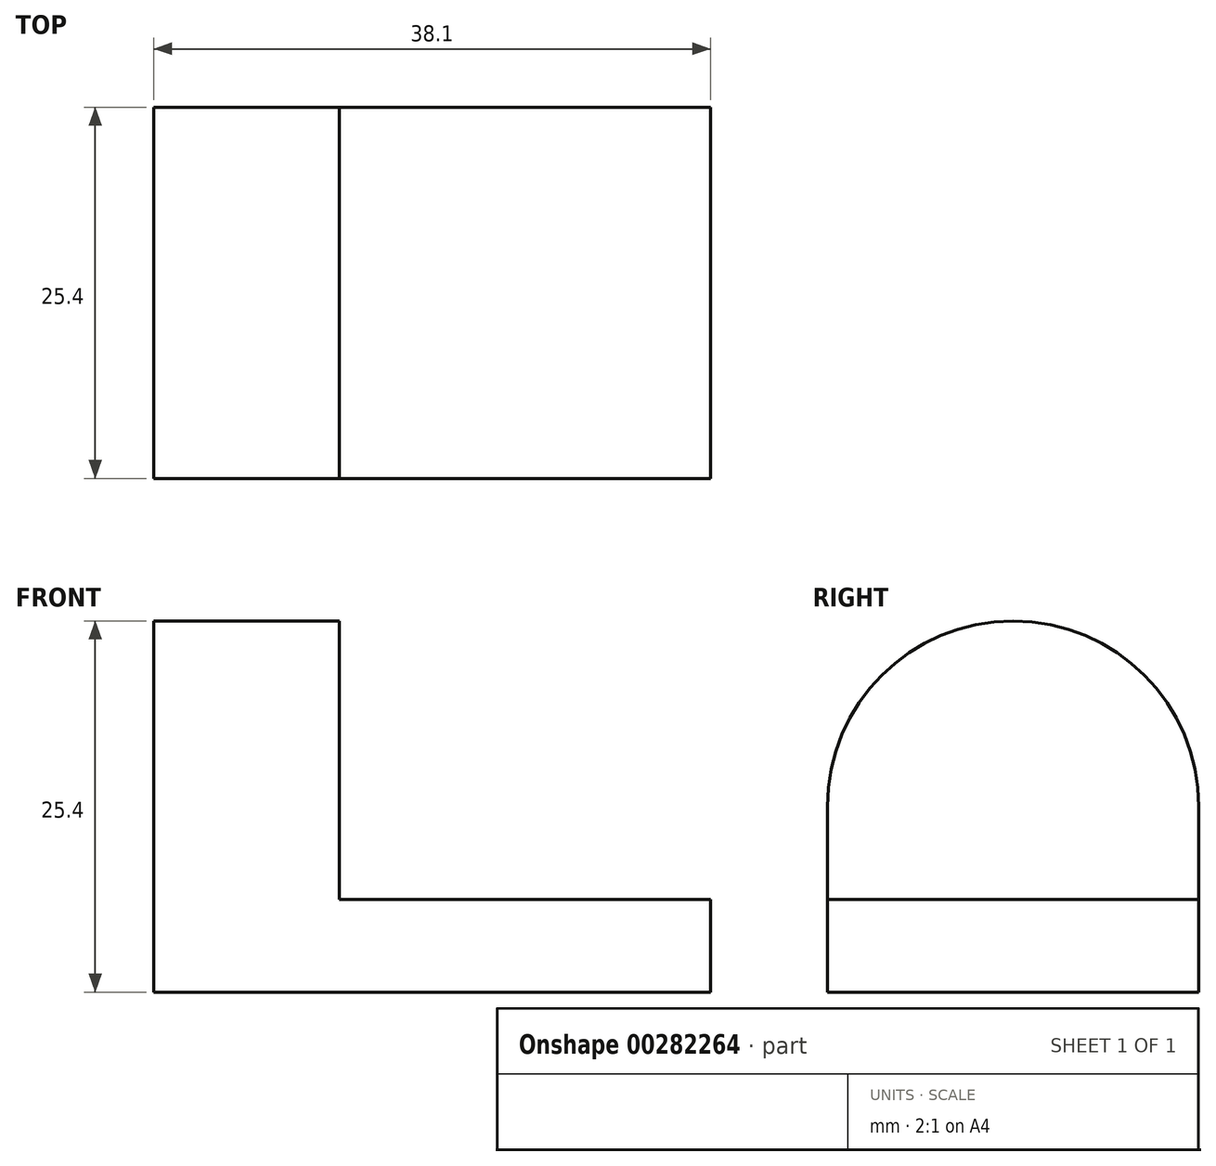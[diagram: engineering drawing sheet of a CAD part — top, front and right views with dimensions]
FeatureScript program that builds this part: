
annotation { "Feature Type Name" : "Feature", "Feature Type Description" : "" }
export const myFeature = defineFeature(function(context is Context, id is Id, definition is map)
    precondition{}
    {
        {
            var Q0;
            Q0=qCreatedBy(makeId("Top.planeOp"),FACE);
            var sketch = newSketch(context, id + "F0", { "sketchPlane" : qUnion([Q0])});
            skLineSegment(sketch, "E0.bottom", {"start": v(0, 0) * mm, "end": v(38.1, 0) * mm});
            skLineSegment(sketch, "E0.top", {"start": v(0, 25.4) * mm, "end": v(38.1, 25.4) * mm});
            skLineSegment(sketch, "E0.left", {"start": v(0, 0) * mm, "end": v(0, 25.4) * mm});
            skLineSegment(sketch, "E0.right", {"start": v(38.1, 0) * mm, "end": v(38.1, 25.4) * mm});
            skSolve(sketch);
        }
        {
            var Q0;
            Q0 = qSketchRegion(id + "F0", true);
            extrude(context, id + "F1", {"entities" : qUnion([Q0]), "depth" : 25.4 * mm});
        }
        {
            var Q0;
            Q0=makeQuery(id+"F1.opExtrude","SWEPT_FACE",FACE,{"disambiguationData":[OSD([sQuery(id+"F0.wireOp",EDGE,"E0.right")])]});
            var sketch = newSketch(context, id + "F2", { "sketchPlane" : qUnion([Q0])});
            skArc(sketch, "E1", {"start": v(25.4, 12.7) * mm, "mid": v(12.7, 25.4) * mm, "end": v(0, 12.7) * mm});
            skLineSegment(sketch, "E2", {"start": v(0, 0) * mm, "end": v(0, 6.35) * mm, "construction": true});
            skLineSegment(sketch, "E3", {"start": v(0, 6.35) * mm, "end": v(25.4, 6.35) * mm});
            skSolve(sketch);
        }
        {
            var Q0;
            {var subQ0=sQuery(id+"F2.wireOp",EDGE,"E1");var subQ1=sQuery(id+"F0.wireOp",EDGE,"E0.right");var subQ4=makeQuery(id+"F1.opExtrude","CAP_EDGE",EDGE,{"disambiguationData":[OSD([subQ1])],"isStart":false});var subQ5=makeQuery(id+"F2.imprint","INTERSECT",VERTEX,{"derivedFrom":[subQ4,subQ0]});Q0=makeQuery(id+"F2.imprint","IMPRINT",FACE,{"disambiguationData":[TD([[makeQuery(id+"F2.imprint","IMPRINT",EDGE,{"disambiguationData":[TD([[subQ5,1.0]])],"derivedFrom":subQ4}),-1.0]])]});}
            extrude(context, id + "F3", {"entities" : qUnion([Q0]), "operationType" : NewBodyOperationType.REMOVE, "endBound" : BoundingType.THROUGH_ALL, "oppositeDirection" : true, "depth" : 25.4 * mm});
        }
        {
            var Q0;
            {var subQ0=sQuery(id+"F2.wireOp",EDGE,"E1");var subQ1=sQuery(id+"F0.wireOp",EDGE,"E0.right");var subQ4=makeQuery(id+"F1.opExtrude","CAP_EDGE",EDGE,{"disambiguationData":[OSD([subQ1])],"isStart":false});var subQ5=makeQuery(id+"F2.imprint","INTERSECT",VERTEX,{"derivedFrom":[subQ4,subQ0]});Q0=makeQuery(id+"F2.imprint","IMPRINT",FACE,{"disambiguationData":[TD([[makeQuery(id+"F2.imprint","IMPRINT",EDGE,{"disambiguationData":[TD([[subQ5,-1.0]])],"derivedFrom":subQ4}),-1.0]])]});}
            extrude(context, id + "F4", {"entities" : qUnion([Q0]), "operationType" : NewBodyOperationType.REMOVE, "endBound" : BoundingType.THROUGH_ALL, "oppositeDirection" : true, "depth" : 25.4 * mm});
        }
        {
            var Q0;
            {var subQ0=sQuery(id+"F2.wireOp",EDGE,"E3");Q0=makeQuery(id+"F2.imprint","IMPRINT",FACE,{"disambiguationData":[TD([[makeQuery(id+"F2.imprint","IMPRINT",EDGE,{"derivedFrom":subQ0}),1.0]])]});}
            extrude(context, id + "F5", {"entities" : qUnion([Q0]), "operationType" : NewBodyOperationType.REMOVE, "oppositeDirection" : true, "depth" : 25.4 * mm});
        }
    });
